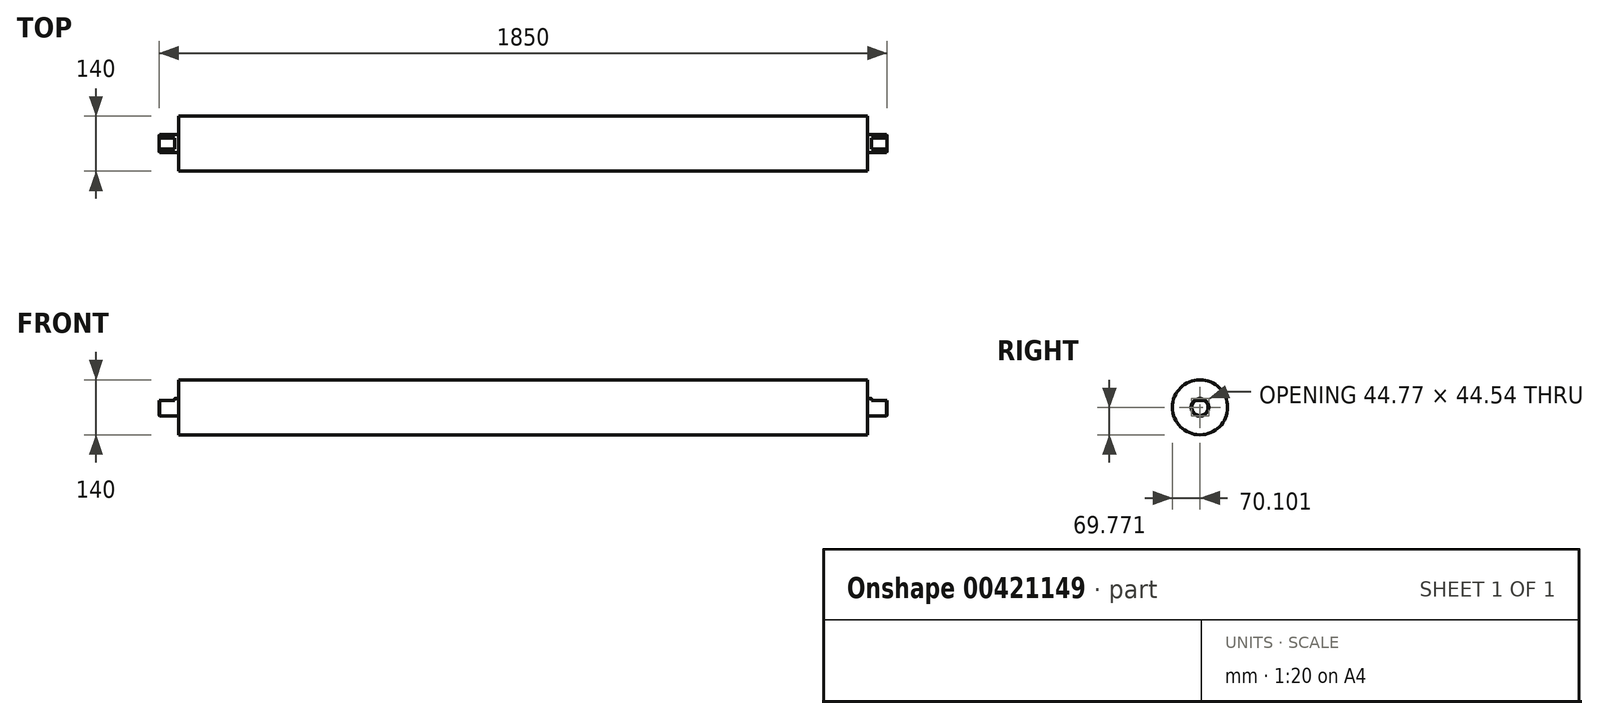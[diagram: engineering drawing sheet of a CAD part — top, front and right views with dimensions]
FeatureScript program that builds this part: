
annotation { "Feature Type Name" : "Feature", "Feature Type Description" : "" }
export const myFeature = defineFeature(function(context is Context, id is Id, definition is map)
    precondition{}
    {
        {
            var Q0;
            Q0=qCreatedBy(makeId("Right.planeOp"),FACE);
            var sketch = newSketch(context, id + "F0", { "sketchPlane" : qUnion([Q0])});
            skCircle(sketch, "E0", {"center": v(0, 0) * mm, "radius": 27.5 * mm});
            skSolve(sketch);
        }
        {
            var Q0;
            Q0=qSketchRegion(id+"F0",true);
            extrude(context, id + "F1", {"entities" : qUnion([Q0]), "endBound" : BoundingType.SYMMETRIC, "depth" : 1750 * mm});
        }
        {
            var Q0;
            Q0=makeQuery(id+"F1.opExtrude","CAP_FACE",FACE,{"disambiguationData":[OSD([sQuery(id+"F0.wireOp",EDGE,"E0")])],"isStart":false});
            var sketch = newSketch(context, id + "F2", { "sketchPlane" : qUnion([Q0])});
            skCircle(sketch, "E1.0.0", {"center": v(0, 0) * mm, "radius": 27.5 * mm, "construction": true});
            skCircle(sketch, "E2", {"center": v(0, 0) * mm, "radius": 22.5 * mm});
            skSolve(sketch);
        }
        {
            var Q0;
            Q0=makeQuery(id+"F2.imprint","IMPRINT",FACE,{"disambiguationData":[TD([[makeQuery(id+"F2.imprint","IMPRINT",EDGE,{"derivedFrom":sQuery(id+"F2.wireOp",EDGE,"E2")}),1.0]])]});
            extrude(context, id + "F3", {"entities" : qUnion([Q0]), "depth" : 50 * mm});
        }
        {
            var Q0;
            Q0=makeQuery(id+"F3.opExtrude","CAP_FACE",FACE,{"disambiguationData":[OSD([sQuery(id+"F2.wireOp",EDGE,"E2")])],"isStart":false});
            var sketch = newSketch(context, id + "F4", { "sketchPlane" : qUnion([Q0])});
            skArc(sketch, "E3.0.0", {"start": v(14.14, 17.5) * mm, "mid": v(0, 22.5) * mm, "end": v(-14.14, 17.5) * mm});
            skLineSegment(sketch, "E4", {"start": v(0, 0) * mm, "end": v(0, 22.5) * mm, "construction": true});
            skLineSegment(sketch, "E5", {"start": v(0, 22.5) * mm, "end": v(35.81, 22.5) * mm, "construction": true});
            skLineSegment(sketch, "E6.0", {"start": v(-14.14, 17.5) * mm, "end": v(14.14, 17.5) * mm});
            skSolve(sketch);
        }
        {
            var Q0;
            Q0=qSketchRegion(id+"F4",true);
            extrude(context, id + "F5", {"entities" : qUnion([Q0]), "operationType" : NewBodyOperationType.REMOVE, "oppositeDirection" : true, "depth" : 40 * mm});
        }
        {
            var Q0;
            Q0=makeQuery(id+"F3.opExtrude","CAP_EDGE",EDGE,{"disambiguationData":[OSD([sQuery(id+"F2.wireOp",EDGE,"E2")])],"isStart":false});
            chamfer(context, id + "F6", {"entities" : qUnion([Q0]), "width" : 2 * mm, "tangentPropagation" : true});
        }
        {
            var Q0;
            Q0=makeQuery(id+"F3.opExtrude","SWEPT_BODY",BODY,{"disambiguationData":[OSD([sQuery(id+"F2.wireOp",EDGE,"E2")])]});
            var Q1;
            Q1=qCreatedBy(makeId("Right.planeOp"),FACE);
            mirror(context, id + "F7", {"operationType" : NewBodyOperationType.ADD, "entities" : qUnion([Q0]), "mirrorPlane" : qUnion([Q1])});
        }
        {
            var Q0;
            Q0=qCreatedBy(makeId("Right.planeOp"),FACE);
            var sketch = newSketch(context, id + "F8", { "sketchPlane" : qUnion([Q0])});
            skCircle(sketch, "E7", {"center": v(0, 0) * mm, "radius": 70 * mm});
            skSolve(sketch);
        }
        {
            var Q0;
            Q0=qSketchRegion(id+"F8",true);
            extrude(context, id + "F9", {"entities" : qUnion([Q0]), "operationType" : NewBodyOperationType.ADD, "endBound" : BoundingType.SYMMETRIC, "depth" : 1750 * mm});
        }
    });
